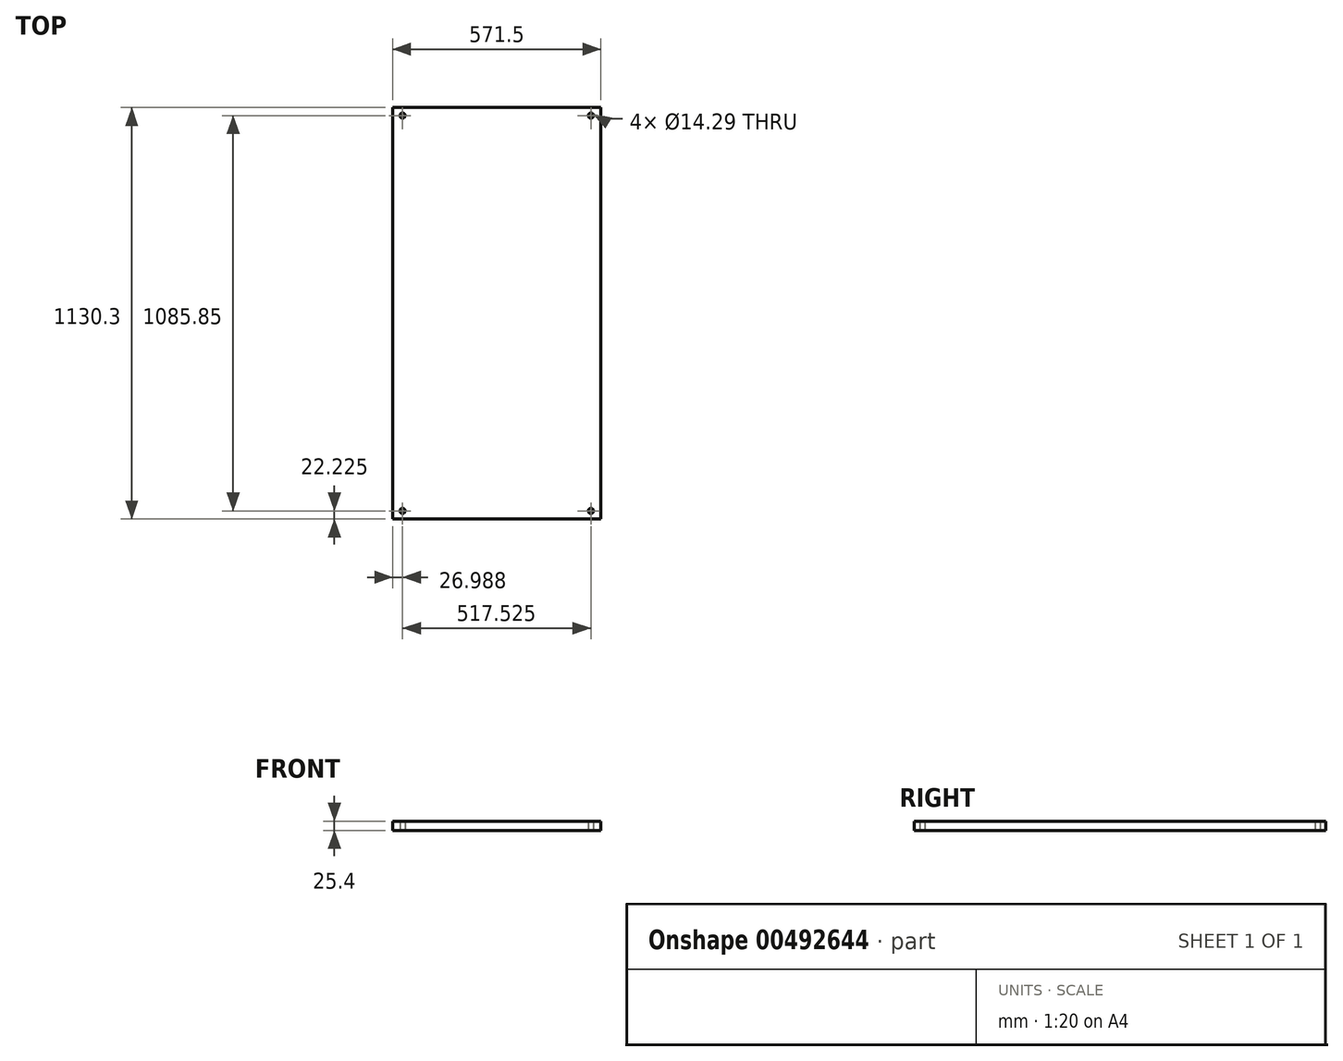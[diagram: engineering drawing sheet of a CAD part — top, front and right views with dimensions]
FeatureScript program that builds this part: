
annotation { "Feature Type Name" : "Feature", "Feature Type Description" : "" }
export const myFeature = defineFeature(function(context is Context, id is Id, definition is map)
    precondition{}
    {
        {
            var Q0;
            Q0=qCreatedBy(makeId("Top.planeOp"),FACE);
            var sketch = newSketch(context, id + "F0", { "sketchPlane" : qUnion([Q0])});
            skLineSegment(sketch, "E0.bottom", {"start": v(285.75, -565.15) * mm, "end": v(-285.75, -565.15) * mm});
            skLineSegment(sketch, "E0.top", {"start": v(285.75, 565.15) * mm, "end": v(-285.75, 565.15) * mm});
            skLineSegment(sketch, "E0.left", {"start": v(285.75, -565.15) * mm, "end": v(285.75, 565.15) * mm});
            skLineSegment(sketch, "E0.right", {"start": v(-285.75, -565.15) * mm, "end": v(-285.75, 565.15) * mm});
            skPoint(sketch, "E0.middle", {"position": v(0, 0) * mm});
            skLineSegment(sketch, "E1", {"start": v(-285.75, 0) * mm, "end": v(285.75, 0) * mm, "construction": true});
            skLineSegment(sketch, "E2", {"start": v(-285.75, 542.92) * mm, "end": v(285.75, 542.93) * mm, "construction": true});
            skCircle(sketch, "E3", {"center": v(-258.76, 542.93) * mm, "radius": 7.14 * mm});
            skCircle(sketch, "E4", {"center": v(258.76, 542.93) * mm, "radius": 7.14 * mm});
            skLineSegment(sketch, "E5", {"start": v(0, -565.15) * mm, "end": v(0, 565.15) * mm, "construction": true});
            skCircle(sketch, "E6.MirrorC", {"center": v(-258.76, -542.93) * mm, "radius": 7.14 * mm});
            skCircle(sketch, "E7.MirrorC", {"center": v(258.76, -542.93) * mm, "radius": 7.14 * mm});
            skSolve(sketch);
        }
        {
            var Q0;
            Q0 = qSketchRegion(id + "F0", true);
            extrude(context, id + "F1", {"entities" : qUnion([Q0]), "depth" : 25.4 * mm, "offsetDistance" : 25.4 * mm});
        }
    });
